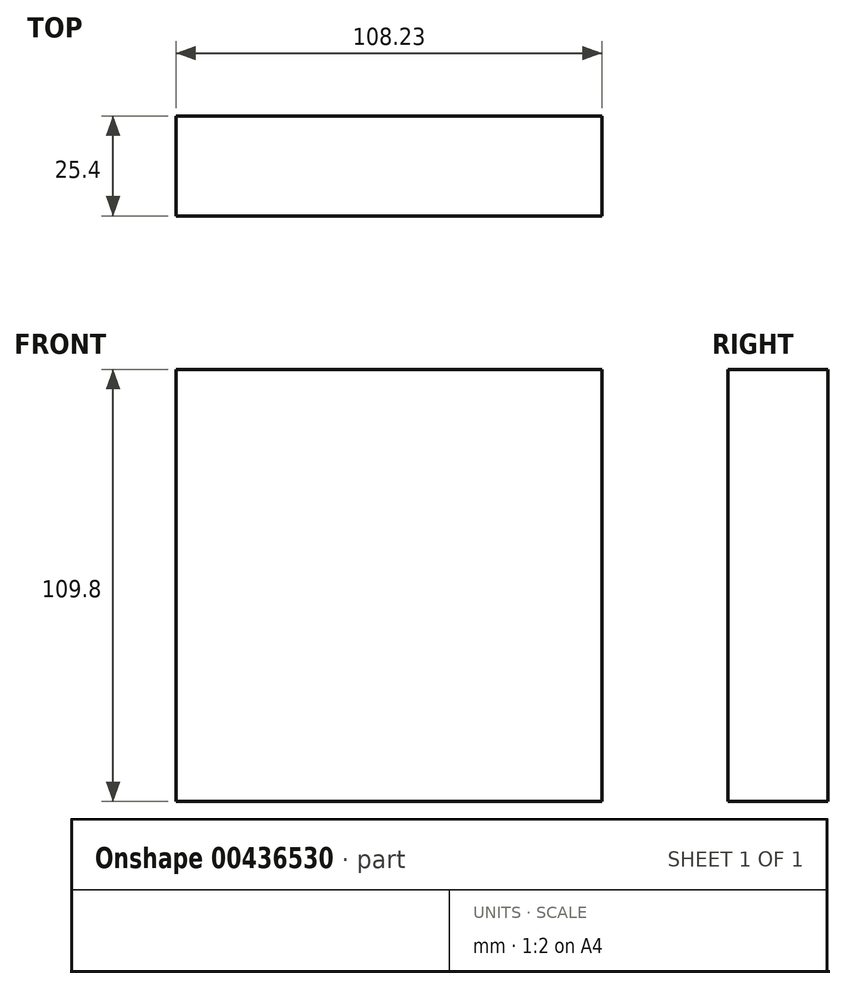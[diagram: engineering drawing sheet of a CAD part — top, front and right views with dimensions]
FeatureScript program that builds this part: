
annotation { "Feature Type Name" : "Feature", "Feature Type Description" : "" }
export const myFeature = defineFeature(function(context is Context, id is Id, definition is map)
    precondition{}
    {
        {
            var Q0;
            Q0=qCreatedBy(makeId("Front.planeOp"),FACE);
            var sketch = newSketch(context, id + "F0", { "sketchPlane" : qUnion([Q0])});
            skLineSegment(sketch, "E0", {"start": v(-57.8, -26.13) * mm, "end": v(50.43, -26.13) * mm});
            skLineSegment(sketch, "E1", {"start": v(50.43, -26.13) * mm, "end": v(50.43, 83.67) * mm});
            skLineSegment(sketch, "E2", {"start": v(50.43, 83.67) * mm, "end": v(-57.8, 83.67) * mm});
            skLineSegment(sketch, "E3", {"start": v(-57.8, 83.67) * mm, "end": v(-57.8, -26.13) * mm});
            skSolve(sketch);
        }
        {
            var Q0;
            Q0 = qSketchRegion(id + "F0", true);
            extrude(context, id + "F1", {"entities" : qUnion([Q0]), "depth" : 25.4 * mm});
        }
    });
